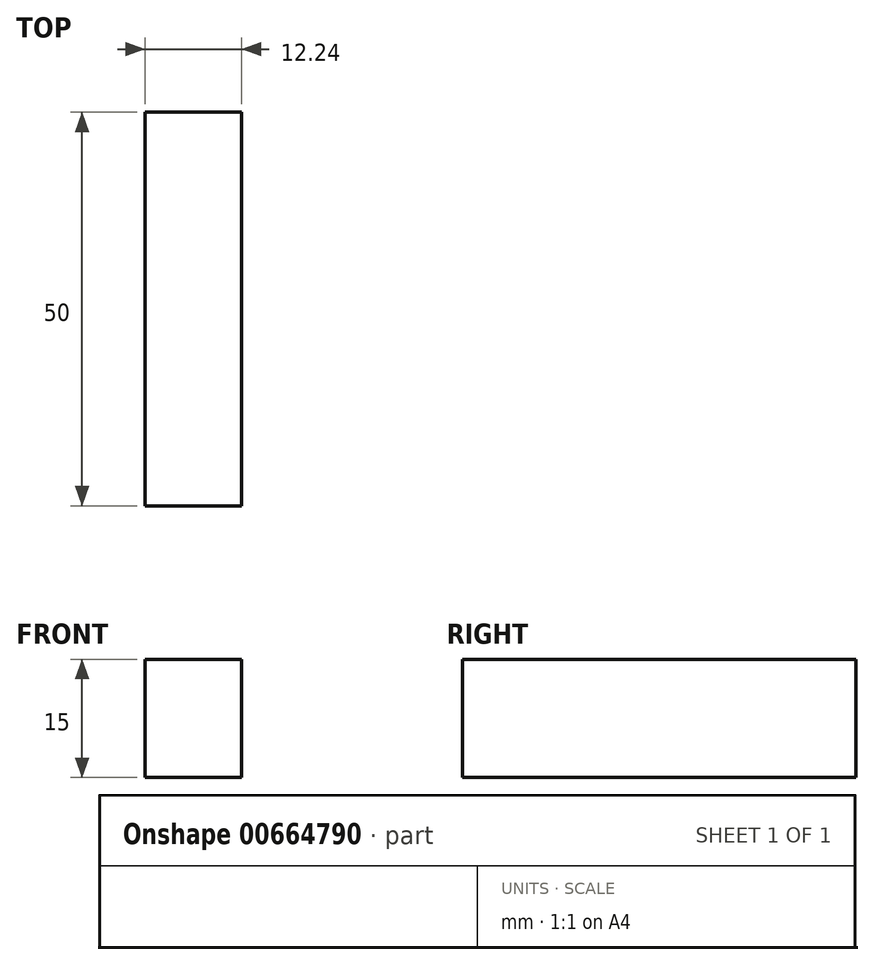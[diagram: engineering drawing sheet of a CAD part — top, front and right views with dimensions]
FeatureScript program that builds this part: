
annotation { "Feature Type Name" : "Feature", "Feature Type Description" : "" }
export const myFeature = defineFeature(function(context is Context, id is Id, definition is map)
    precondition{}
    {
        {
            var Q0;
            Q0=qCreatedBy(makeId("Top.planeOp"),FACE);
            var sketch = newSketch(context, id + "F0", { "sketchPlane" : qUnion([Q0])});
            skLineSegment(sketch, "E0.bottom", {"start": v(6.13, 25) * mm, "end": v(-6.12, 25) * mm});
            skLineSegment(sketch, "E0.top", {"start": v(6.12, -25) * mm, "end": v(-6.13, -25) * mm});
            skLineSegment(sketch, "E0.left", {"start": v(6.13, 25) * mm, "end": v(6.12, -25) * mm});
            skLineSegment(sketch, "E0.right", {"start": v(-6.12, 25) * mm, "end": v(-6.13, -25) * mm});
            skPoint(sketch, "E0.middle", {"position": v(0, 0) * mm});
            skSolve(sketch);
        }
        {
            var Q0;
            Q0=makeQuery(id+"F0.imprint","IMPRINT",FACE,{"disambiguationData":[TD([[makeQuery(id+"F0.imprint","IMPRINT",EDGE,{"derivedFrom":sQuery(id+"F0.wireOp",EDGE,"E0.bottom")}),1.0]])]});
            extrude(context, id + "F1", {"entities" : qUnion([Q0]), "depth" : 15 * mm, "offsetDistance" : 25 * mm});
        }
    });
